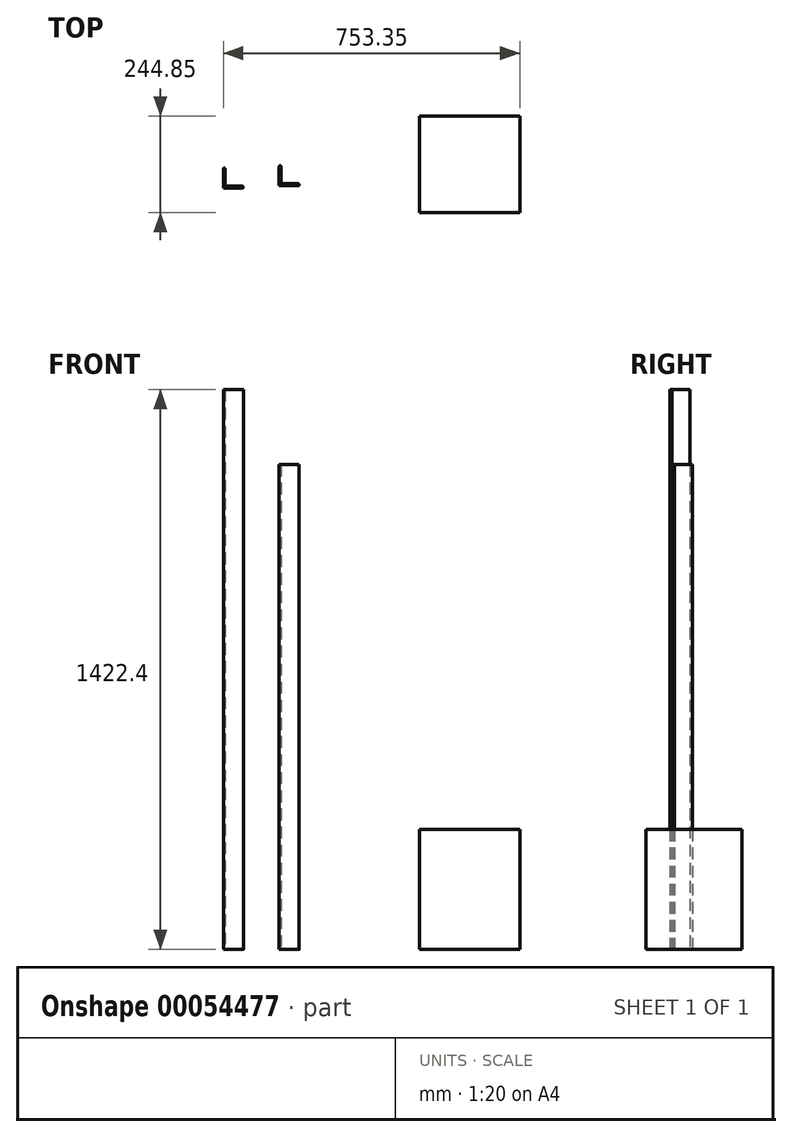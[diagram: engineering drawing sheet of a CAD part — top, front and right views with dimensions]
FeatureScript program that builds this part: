
annotation { "Feature Type Name" : "Feature", "Feature Type Description" : "" }
export const myFeature = defineFeature(function(context is Context, id is Id, definition is map)
    precondition{}
    {
        {
            var Q0;
            Q0=qCreatedBy(makeId("Top.planeOp"),FACE);
            var sketch = newSketch(context, id + "F0", { "sketchPlane" : qUnion([Q0])});
            skLineSegment(sketch, "E0.rect.bottom", {"start": v(-23.02, 25.4) * mm, "end": v(-23.02, 25.4) * mm});
            skLineSegment(sketch, "E0.rect.top", {"start": v(-25.4, -25.4) * mm, "end": v(23.02, -25.4) * mm});
            skLineSegment(sketch, "E0.rect.left", {"start": v(-25.4, 23.02) * mm, "end": v(-25.4, -25.4) * mm});
            skPoint(sketch, "E0.rect.middle", {"position": v(0, 0) * mm});
            skLineSegment(sketch, "E1.0", {"start": v(-18.26, -20.64) * mm, "end": v(23.02, -20.64) * mm});
            skLineSegment(sketch, "E1.1", {"start": v(-20.64, 23.02) * mm, "end": v(-20.64, -18.26) * mm});
            skLineSegment(sketch, "E2", {"start": v(25.4, -20.64) * mm, "end": v(25.4, -20.64) * mm});
            skLineSegment(sketch, "E3", {"start": v(25.4, -23.02) * mm, "end": v(25.4, -23.02) * mm});
            skPoint(sketch, "E4.visualSharp", {"position": v(-25.4, 25.4) * mm});
            skArc(sketch, "E4.filletArc", {"start": v(-23.02, 25.4) * mm, "mid": v(-24.7, 24.7) * mm, "end": v(-25.4, 23.02) * mm});
            skPoint(sketch, "E5.visualSharp", {"position": v(-20.64, 25.4) * mm});
            skArc(sketch, "E5.filletArc", {"start": v(-20.64, 23.02) * mm, "mid": v(-21.33, 24.7) * mm, "end": v(-23.02, 25.4) * mm});
            skPoint(sketch, "E6.visualSharp", {"position": v(-20.64, -20.64) * mm});
            skArc(sketch, "E6.filletArc", {"start": v(-20.64, -18.26) * mm, "mid": v(-19.94, -19.94) * mm, "end": v(-18.26, -20.64) * mm});
            skPoint(sketch, "E7.visualSharp", {"position": v(25.4, -20.64) * mm});
            skArc(sketch, "E7.filletArc", {"start": v(25.4, -23.02) * mm, "mid": v(24.7, -21.33) * mm, "end": v(23.02, -20.64) * mm});
            skPoint(sketch, "E8.visualSharp", {"position": v(25.4, -25.4) * mm});
            skArc(sketch, "E8.filletArc", {"start": v(23.02, -25.4) * mm, "mid": v(24.7, -24.7) * mm, "end": v(25.4, -23.02) * mm});
            skLineSegment(sketch, "E9.rect.top", {"start": v(116.8, -19.32) * mm, "end": v(165.22, -19.32) * mm});
            skLineSegment(sketch, "E10", {"start": v(167.6, -14.56) * mm, "end": v(167.6, -14.56) * mm});
            skPoint(sketch, "E11.visualSharp", {"position": v(167.6, -19.32) * mm});
            skPoint(sketch, "E9.rect.middle", {"position": v(142.2, 6.08) * mm});
            skPoint(sketch, "E12.visualSharp", {"position": v(121.56, -14.56) * mm});
            skLineSegment(sketch, "E13.1", {"start": v(121.56, 29.1) * mm, "end": v(121.56, -12.17) * mm});
            skPoint(sketch, "E14.visualSharp", {"position": v(116.8, 31.48) * mm});
            skLineSegment(sketch, "E13.0", {"start": v(123.94, -14.56) * mm, "end": v(165.22, -14.56) * mm});
            skLineSegment(sketch, "E9.rect.bottom", {"start": v(119.18, 31.48) * mm, "end": v(119.18, 31.48) * mm});
            skLineSegment(sketch, "E9.rect.left", {"start": v(116.8, 29.1) * mm, "end": v(116.8, -19.32) * mm});
            skPoint(sketch, "E15.visualSharp", {"position": v(121.56, 31.48) * mm});
            skPoint(sketch, "E16.visualSharp", {"position": v(167.6, -14.56) * mm});
            skArc(sketch, "E11.filletArc", {"start": v(165.22, -19.32) * mm, "mid": v(166.9, -18.62) * mm, "end": v(167.6, -16.94) * mm});
            skArc(sketch, "E12.filletArc", {"start": v(121.56, -12.17) * mm, "mid": v(122.26, -13.86) * mm, "end": v(123.94, -14.56) * mm});
            skArc(sketch, "E15.filletArc", {"start": v(121.56, 29.1) * mm, "mid": v(120.86, 30.78) * mm, "end": v(119.18, 31.48) * mm});
            skArc(sketch, "E14.filletArc", {"start": v(119.18, 31.48) * mm, "mid": v(117.5, 30.78) * mm, "end": v(116.8, 29.1) * mm});
            skArc(sketch, "E16.filletArc", {"start": v(167.6, -16.94) * mm, "mid": v(166.9, -15.25) * mm, "end": v(165.22, -14.56) * mm});
            skLineSegment(sketch, "E17", {"start": v(167.6, -16.94) * mm, "end": v(167.6, -16.94) * mm});
            skLineSegment(sketch, "E18.bottom", {"start": v(727.95, -87.33) * mm, "end": v(472.75, -87.33) * mm});
            skLineSegment(sketch, "E18.top", {"start": v(727.95, 157.52) * mm, "end": v(472.75, 157.52) * mm});
            skLineSegment(sketch, "E18.left", {"start": v(727.95, -87.33) * mm, "end": v(727.95, 157.52) * mm});
            skLineSegment(sketch, "E18.right", {"start": v(472.75, -87.33) * mm, "end": v(472.75, 157.52) * mm});
            skSolve(sketch);
        }
        {
            var Q0;
            Q0=makeQuery(id+"F0.imprint","IMPRINT",FACE,{"disambiguationData":[TD([[makeQuery(id+"F0.imprint","IMPRINT",EDGE,{"derivedFrom":sQuery(id+"F0.wireOp",EDGE,"E0.rect.top")}),1.0]])]});
            extrude(context, id + "F1", {"entities" : qUnion([Q0]), "depth" : 1422.4 * mm});
        }
        {
            var Q0;
            Q0=makeQuery(id+"F0.imprint","IMPRINT",FACE,{"disambiguationData":[TD([[makeQuery(id+"F0.imprint","IMPRINT",EDGE,{"derivedFrom":sQuery(id+"F0.wireOp",EDGE,"E9.rect.top")}),1.0]])]});
            extrude(context, id + "F2", {"entities" : qUnion([Q0]), "depth" : 1231.9 * mm});
        }
        {
            var Q0;
            Q0=makeQuery(id+"F0.imprint","IMPRINT",FACE,{"disambiguationData":[TD([[makeQuery(id+"F0.imprint","IMPRINT",EDGE,{"derivedFrom":sQuery(id+"F0.wireOp",EDGE,"E18.bottom")}),-1.0]])]});
            extrude(context, id + "F3", {"entities" : qUnion([Q0]), "depth" : 304.8 * mm});
        }
    });
